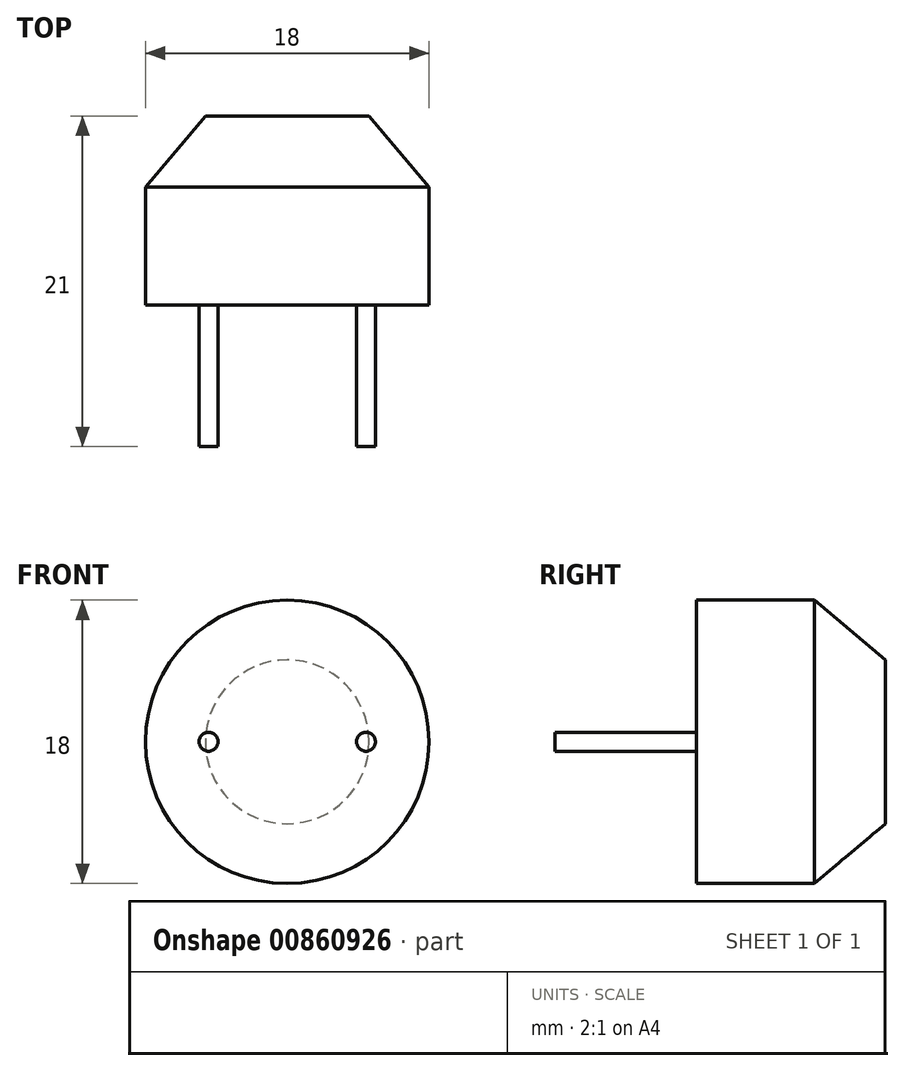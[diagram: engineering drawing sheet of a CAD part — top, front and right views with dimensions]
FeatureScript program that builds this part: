
annotation { "Feature Type Name" : "Feature", "Feature Type Description" : "" }
export const myFeature = defineFeature(function(context is Context, id is Id, definition is map)
    precondition{}
    {
        {
            var Q0;
            Q0=qCreatedBy(makeId("Front.planeOp"),FACE);
            var sketch = newSketch(context, id + "F0", { "sketchPlane" : qUnion([Q0])});
            skCircle(sketch, "E0", {"center": v(0, 0) * mm, "radius": 9 * mm});
            skSolve(sketch);
        }
        {
            var Q0;
            Q0 = qSketchRegion(id + "F0", true);
            extrude(context, id + "F1", {"entities" : qUnion([Q0]), "depth" : 12 * mm, "offsetDistance" : 25 * mm});
        }
        {
            var Q0;
            Q0=makeQuery(id+"F1.opExtrude","CAP_EDGE",EDGE,{"disambiguationData":[OSD([sQuery(id+"F0.wireOp",EDGE,"E0")])],"isStart":true});
            chamfer(context, id + "F2", {"entities" : qUnion([Q0]), "chamferType" : ChamferType.OFFSET_ANGLE, "width" : 3.8 * mm, "oppositeDirection" : true, "angle" : 50 * degree, "tangentPropagation" : true});
        }
        {
            var Q0;
            Q0=makeQuery(id+"F1.opExtrude","CAP_FACE",FACE,{"disambiguationData":[OSD([sQuery(id+"F0.wireOp",EDGE,"E0")])],"isStart":false});
            var sketch = newSketch(context, id + "F3", { "sketchPlane" : qUnion([Q0])});
            skCircle(sketch, "E1", {"center": v(-5, 0) * mm, "radius": 0.6 * mm});
            skCircle(sketch, "E2", {"center": v(5, 0) * mm, "radius": 0.6 * mm});
            skSolve(sketch);
        }
        {
            var Q0;
            Q0 = qSketchRegion(id + "F3", true);
            extrude(context, id + "F4", {"entities" : qUnion([Q0]), "operationType" : NewBodyOperationType.ADD, "depth" : 9 * mm, "offsetDistance" : 25 * mm});
        }
    });
